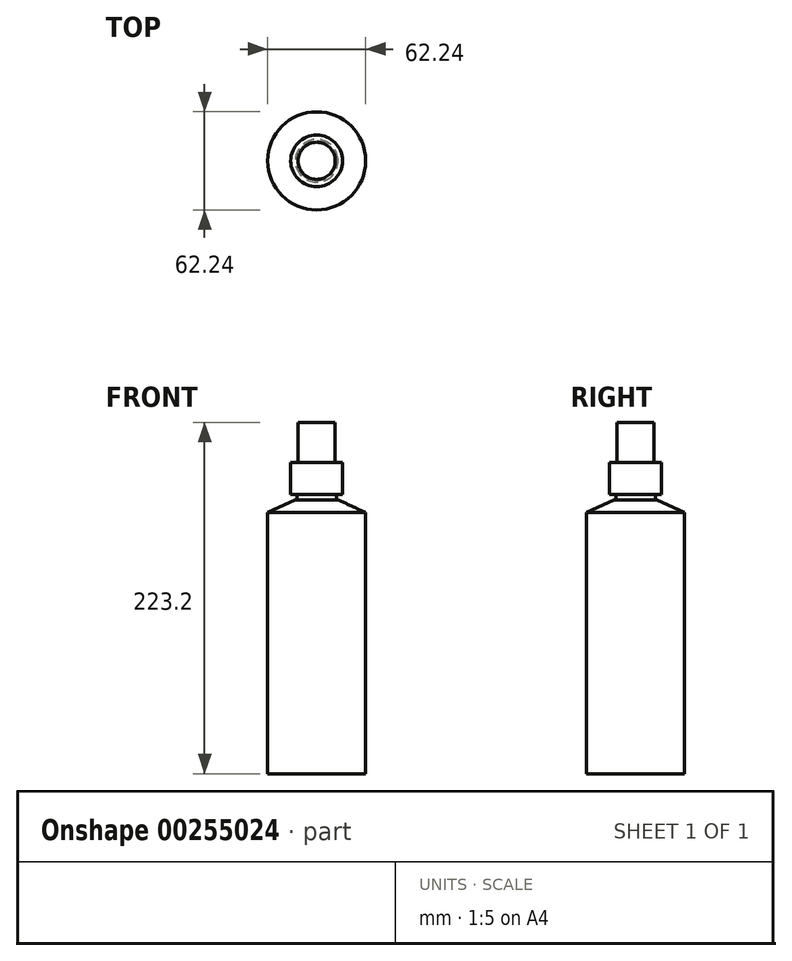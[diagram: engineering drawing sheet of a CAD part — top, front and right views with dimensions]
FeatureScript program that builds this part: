
annotation { "Feature Type Name" : "Feature", "Feature Type Description" : "" }
export const myFeature = defineFeature(function(context is Context, id is Id, definition is map)
    precondition{}
    {
        {
            var Q0;
            Q0=qCreatedBy(makeId("Top.planeOp"),FACE);
            var sketch = newSketch(context, id + "F0", { "sketchPlane" : qUnion([Q0])});
            skCircle(sketch, "E0", {"center": v(0, 0) * mm, "radius": 31.12 * mm});
            skSolve(sketch);
        }
        {
            var Q0;
            Q0=makeQuery(id+"F0.imprint","IMPRINT",FACE,{"disambiguationData":[TD([[makeQuery(id+"F0.imprint","IMPRINT",EDGE,{"derivedFrom":sQuery(id+"F0.wireOp",EDGE,"E0")}),1.0]])]});
            extrude(context, id + "F1", {"entities" : qUnion([Q0]), "depth" : 174 * mm});
        }
        {
            var Q0;
            Q0=makeQuery(id+"F1.opExtrude","CAP_EDGE",EDGE,{"disambiguationData":[OSD([sQuery(id+"F0.wireOp",EDGE,"E0")])],"isStart":false});
            chamfer(context, id + "F2", {"entities" : qUnion([Q0]), "chamferType" : ChamferType.OFFSET_ANGLE, "width" : 17.5 * mm, "oppositeDirection" : false, "angle" : 25 * degree, "tangentPropagation" : true});
        }
        {
            var Q0;
            Q0=makeQuery(id+"F1.opExtrude","CAP_FACE",FACE,{"disambiguationData":[OSD([sQuery(id+"F0.wireOp",EDGE,"E0")])],"isStart":false});
            var sketch = newSketch(context, id + "F3", { "sketchPlane" : qUnion([Q0])});
            skCircle(sketch, "E1", {"center": v(0, 0) * mm, "radius": 12.5 * mm});
            skSolve(sketch);
        }
        {
            var Q0;
            Q0=makeQuery(id+"F3.imprint","IMPRINT",FACE,{"disambiguationData":[TD([[makeQuery(id+"F3.imprint","IMPRINT",EDGE,{"derivedFrom":sQuery(id+"F3.wireOp",EDGE,"E1")}),1.0]])]});
            extrude(context, id + "F4", {"entities" : qUnion([Q0]), "operationType" : NewBodyOperationType.ADD, "depth" : 3.5 * mm});
        }
        {
            var Q0;
            Q0=makeQuery(id+"F4.opExtrude","CAP_FACE",FACE,{"disambiguationData":[OSD([sQuery(id+"F3.wireOp",EDGE,"E1")])],"isStart":false});
            var sketch = newSketch(context, id + "F5", { "sketchPlane" : qUnion([Q0])});
            skCircle(sketch, "E2", {"center": v(0, 0) * mm, "radius": 16.45 * mm});
            skSolve(sketch);
        }
        {
            var Q0;
            Q0 = qSketchRegion(id + "F5", true);
            extrude(context, id + "F6", {"entities" : qUnion([Q0]), "operationType" : NewBodyOperationType.ADD, "depth" : 20.3 * mm});
        }
        {
            var Q0;
            Q0=makeQuery(id+"F6.opExtrude","CAP_FACE",FACE,{"disambiguationData":[OSD([sQuery(id+"F5.wireOp",EDGE,"E2")])],"isStart":false});
            var sketch = newSketch(context, id + "F7", { "sketchPlane" : qUnion([Q0])});
            skCircle(sketch, "E3", {"center": v(0, 0) * mm, "radius": 11.8 * mm});
            skSolve(sketch);
        }
        {
            var Q0;
            Q0 = qSketchRegion(id + "F7", true);
            extrude(context, id + "F8", {"entities" : qUnion([Q0]), "operationType" : NewBodyOperationType.ADD, "depth" : 25.4 * mm});
        }
    });
